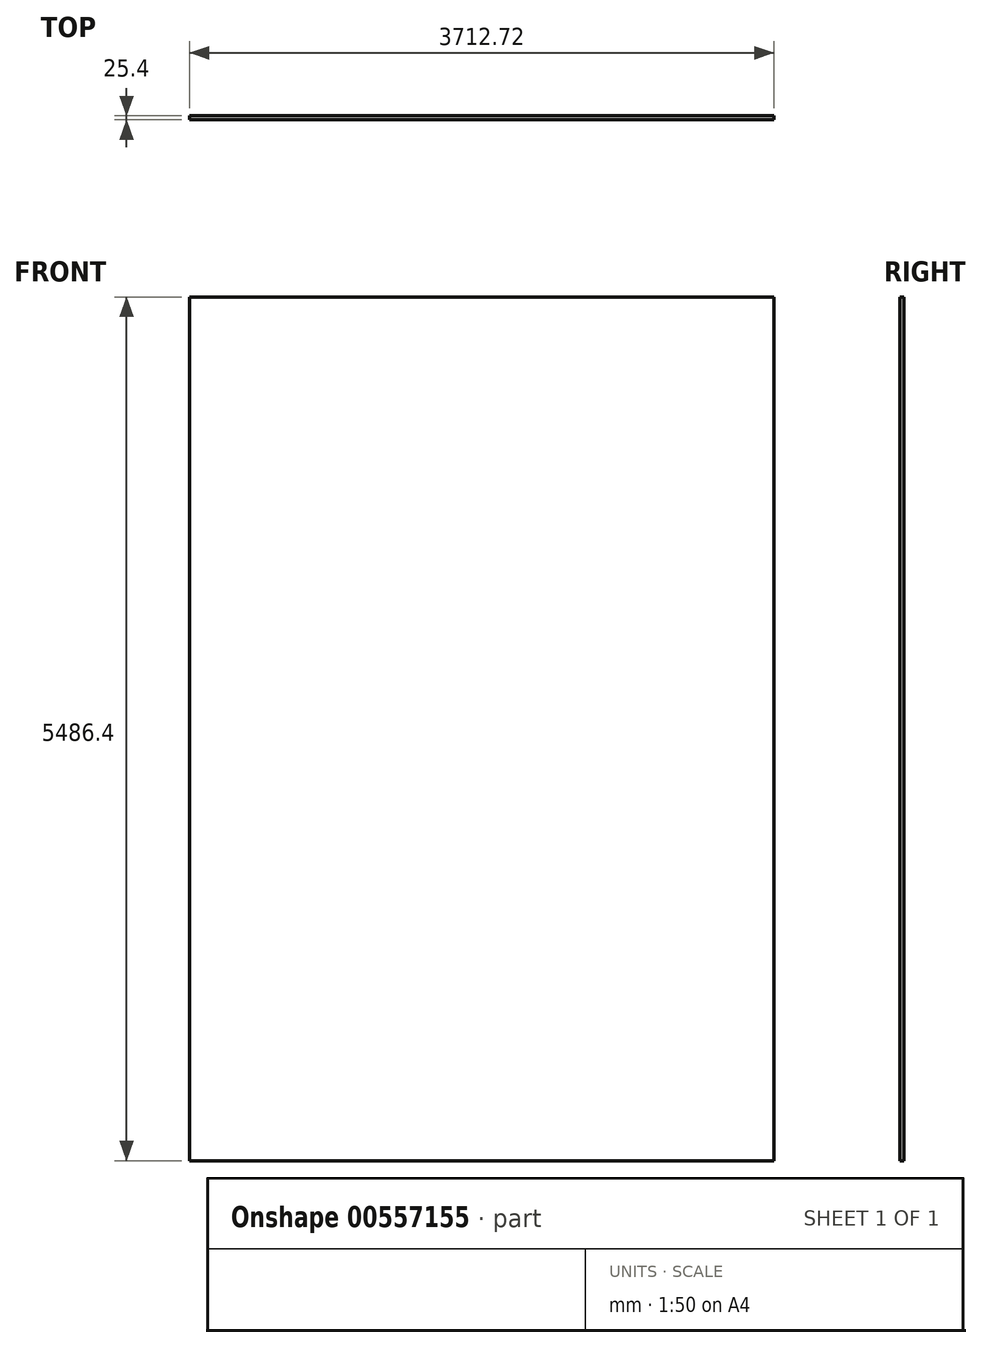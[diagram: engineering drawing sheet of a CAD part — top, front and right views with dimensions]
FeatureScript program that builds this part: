
annotation { "Feature Type Name" : "Feature", "Feature Type Description" : "" }
export const myFeature = defineFeature(function(context is Context, id is Id, definition is map)
    precondition{}
    {
        {
            var Q0;
            Q0=qCreatedBy(makeId("Front.planeOp"),FACE);
            var sketch = newSketch(context, id + "F0", { "sketchPlane" : qUnion([Q0])});
            skLineSegment(sketch, "E0.bottom", {"start": v(-1856.36, 2743.2) * mm, "end": v(1856.36, 2743.2) * mm});
            skLineSegment(sketch, "E0.top", {"start": v(-1856.36, -2743.2) * mm, "end": v(1856.36, -2743.2) * mm});
            skLineSegment(sketch, "E0.left", {"start": v(-1856.36, 2743.2) * mm, "end": v(-1856.36, -2743.2) * mm});
            skLineSegment(sketch, "E0.right", {"start": v(1856.36, 2743.2) * mm, "end": v(1856.36, -2743.2) * mm});
            skPoint(sketch, "E0.middle", {"position": v(0, 0) * mm});
            skLineSegment(sketch, "E1", {"start": v(0, 2743.2) * mm, "end": v(0, -2743.2) * mm, "construction": true});
            skSolve(sketch);
        }
        {
            var Q0;
            Q0 = qSketchRegion(id + "F0", true);
            extrude(context, id + "F1", {"entities" : qUnion([Q0]), "depth" : 25.4 * mm, "offsetDistance" : 25.4 * mm});
        }
    });
